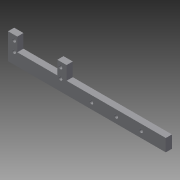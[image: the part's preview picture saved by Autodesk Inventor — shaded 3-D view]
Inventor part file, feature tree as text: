
AUTODESK INVENTOR PART (.ipt)
format: ipt  version: 2015 (Build 190159000, 159)  size: 102,400 bytes
history: native  units: in
note: dims shown in document units (in); Inventor stores cm internally (conversion verified against a paired STEP export)
features: extrude x1, sketch x1
ambient origin geometry x8: Origin, YZ Plane, XZ Plane, XY Plane, X Axis, Y Axis, Z Axis, Center Point
bodies: Solid1 (feature_tree)
feature tree (2):
  extrude  "Extrusion1"  Depth=0.5in
  sketch  "Sketch1"  dims[d0=4.0in d1=0.5in d2=0.1457in d3=0.1457in d4=0.1457in d5=2.3622in d6=0.374in d7=0.5472in d8=0.374in d9=0.547in d12=0.146in d15=0.146in d17=0.146in d19=0.146in d20=0.25in d21=0.0in]
